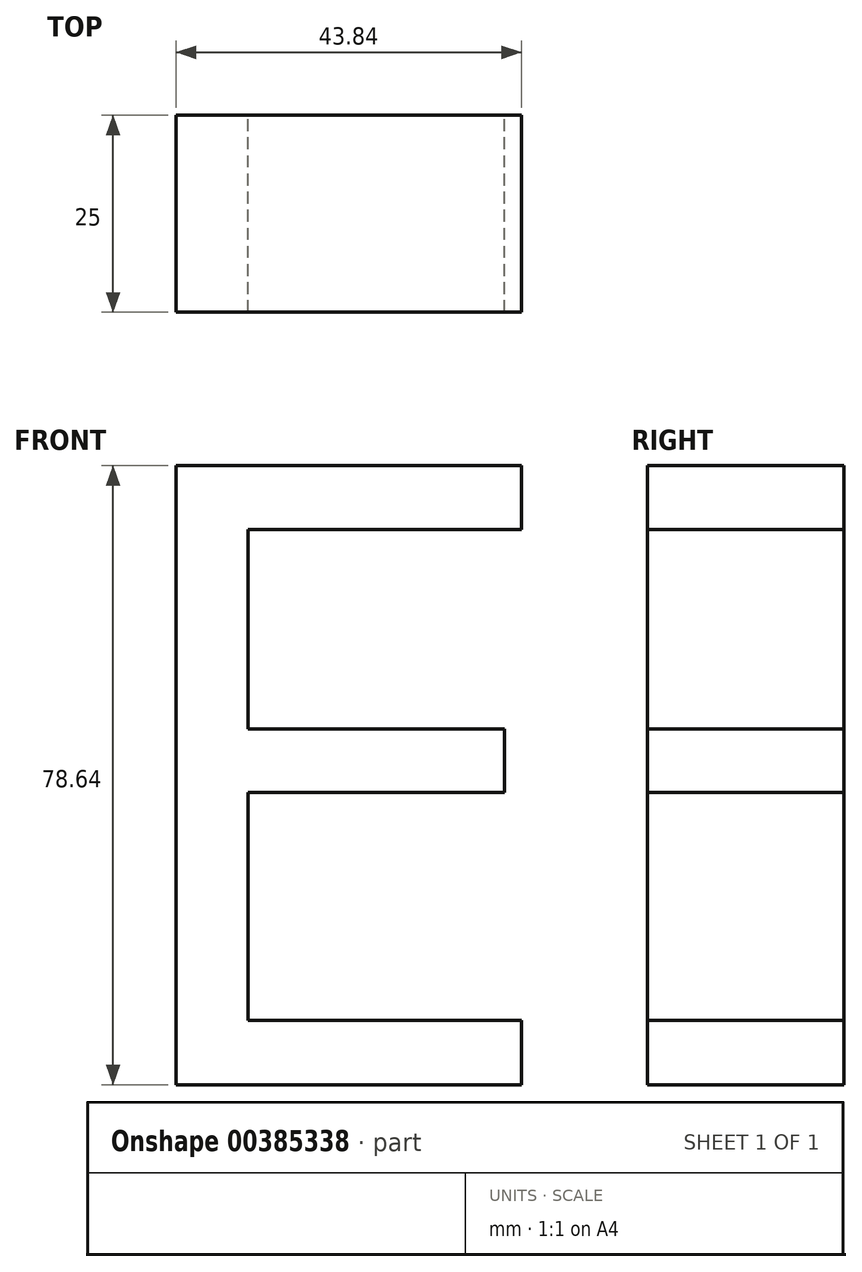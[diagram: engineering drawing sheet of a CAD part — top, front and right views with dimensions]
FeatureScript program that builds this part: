
annotation { "Feature Type Name" : "Feature", "Feature Type Description" : "" }
export const myFeature = defineFeature(function(context is Context, id is Id, definition is map)
    precondition{}
    {
        {
            var Q0;
            Q0=qCreatedBy(makeId("Front.planeOp"),FACE);
            var sketch = newSketch(context, id + "F0", { "sketchPlane" : qUnion([Q0])});
            skText(sketch, "E0", { "text": "E", "fontName": "OpenSans-Regular.ttf"});
            const initialGuessF0  = {"E0": [-0.05683, -0.0357, 1, 0, 0.07931]};
            skSetInitialGuess(sketch, initialGuessF0);
            skSolve(sketch);
        }
        {
            var Q0;
            Q0 = qSketchRegion(id + "F0", true);
            extrude(context, id + "F1", {"entities" : qUnion([Q0]), "depth" : 25 * mm});
        }
    });
